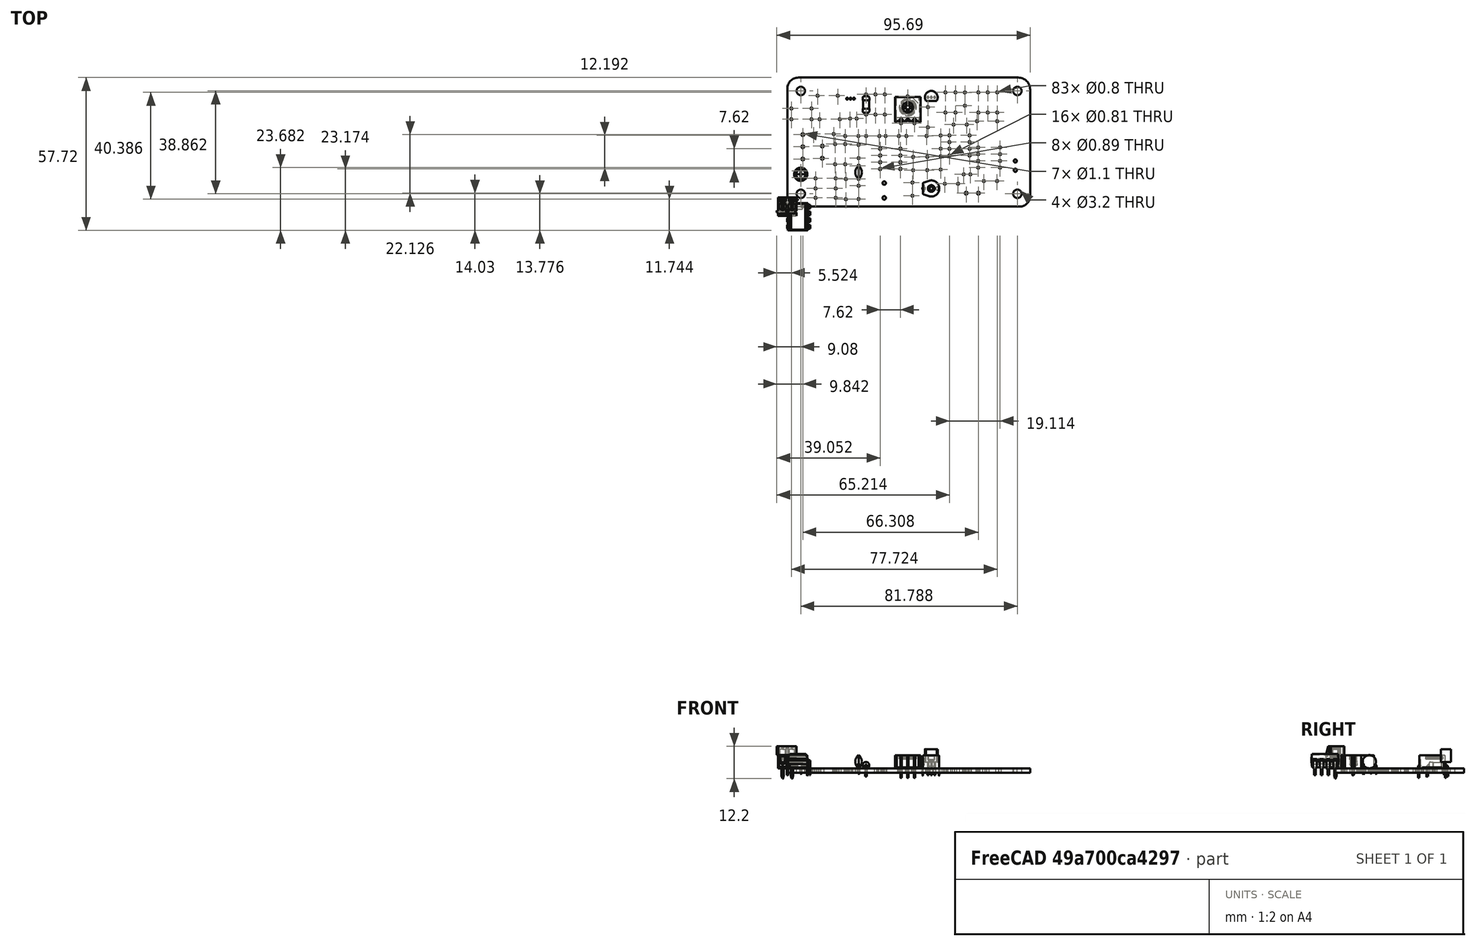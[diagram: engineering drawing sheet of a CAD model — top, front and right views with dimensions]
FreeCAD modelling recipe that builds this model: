
FCSTD DOCUMENT  (FreeCAD 0.19R24267 +148 (Git))
Label: if-and-log-amp-board
License: All rights reserved
LicenseURL: http://en.wikipedia.org/wiki/All_rights_reserved
objects: Part::Feature×57, App::Link×44, App::Part×10, PartDesign::CoordinateSystem×1, Sketcher::SketchObject×1
note: 59 computed .brp shape members not serialized (recipe doc carries the construction recipe); baked Part::Feature solids carry a one-line shape summary decoded from their .brp

FEATURE [PartDesign::CoordinateSystem] Local_CS_cd3
  AttacherType = Attacher::AttachEngine3D
FEATURE [Part::Feature] Pcb_cd3
  Placement = pos=(-95.3516,129.184,0) rot=(0,0,1;0rad)
  shape: bbox 91.69 x 48.77 x 1.6 mm, 140 faces (baked)
FEATURE [Sketcher::SketchObject] PCB_Sketch_cd3
  FullyConstrained = false
  sketch-geometry (8):
    g0: LineSegment StartX=91.694 StartY=3.98868 StartZ=0 EndX=91.694 EndY=44.2582 EndZ=0
    g1: LineSegment StartX=4.55236 StartY=0 StartZ=0 EndX=87.7053 EndY=-2.7e-15 EndZ=0
    g2: LineSegment StartX=0 StartY=44.5614 StartZ=0 EndX=0 EndY=4.55236 EndZ=0
    g3: LineSegment StartX=87.1842 StartY=48.768 StartZ=0 EndX=4.20659 EndY=48.768 EndZ=0
    g4: ArcOfCircle CenterX=4.20659 CenterY=44.5614 CenterZ=0 NormalX=0 NormalY=0 NormalZ=-1 AngleXU=1.7676e-08 Radius=4.20659 StartAngle=0 EndAngle=1.5708
    g5: ArcOfCircle CenterX=87.7053 CenterY=3.98868 CenterZ=0 NormalX=0 NormalY=0 NormalZ=-1 AngleXU=-3.14159 Radius=3.98868 StartAngle=0 EndAngle=1.5708
    g6: ArcOfCircle CenterX=4.55236 CenterY=4.55236 CenterZ=0 NormalX=0 NormalY=0 NormalZ=-1 AngleXU=-1.5708 Radius=4.55236 StartAngle=0 EndAngle=1.5708
    g7: ArcOfCircle CenterX=87.1842 CenterY=44.2582 CenterZ=0 NormalX=0 NormalY=0 NormalZ=-1 AngleXU=1.5708 Radius=4.50978 StartAngle=0 EndAngle=1.5708
  constraints (8):
    c: Coincident(g2,g6)
    c: Coincident(g2,g4)
    c: Coincident(g3,g4)
    c: Coincident(g1,g6)
    c: Coincident(g3,g7)
    c: Coincident(g1,g5)
    c: Coincident(g0,g5)
    c: Coincident(g0,g7)
FEATURE [Part::Feature] Shape  label="R312_R_Axial_DIN0207_L63mm_D25mm_P762mm_Horizontal_d8800c764c18"
  Placement = pos=(29.718,42.418,0) rot=(0,0,-1;1.5708rad)
  shape: bbox 2.706 x 8.418 x 5.603 mm, 15 faces (baked)
FEATURE [App::Link] R312_R_Axial_DIN0207_L63mm_D25mm_P762mm_Horizontal_d8800c764c18_ln_  label="R317_R_Axial_DIN0207_L63mm_D25mm_P762mm_Horizontal_4018a25076d7"
  LinkPlacement = pos=(53.086,37.592,0) rot=(0,0,-1;1.5708rad)
  LinkedObject = -> Shape
  Placement = pos=(53.086,37.592,0) rot=(0,0,-1;1.5708rad)
FEATURE [Part::Feature] Part__Feature  label="T37-6 IND"
  Placement = pos=(0,-2.7,-0.5) rot=(1,0,0;1.5708rad)
  shape: bbox 10.32 x 3.252 x 10.32 mm, 8 faces, 0 solids (baked)
FEATURE [Part::Feature] Part__Feature001  label="T37-6 IND001"
  Placement = pos=(0,-2.7,-0.5) rot=(1,0,0;1.5708rad)
  shape: bbox 10.51 x 3.773 x 9.618 mm, 81 faces, 0 solids (baked)
FEATURE [Part::Feature] Part__Feature002  label="T37-6 IND002"
  Placement = pos=(0,-2.7,-0.5) rot=(1,0,0;1.5708rad)
  shape: bbox 2.23 x 4.584 x 1.894 mm, 1 faces, 0 solids (baked)
FEATURE [Part::Feature] Part__Feature003  label="T37-6 IND003"
  Placement = pos=(0,-2.7,-0.5) rot=(1,0,0;1.5708rad)
  shape: bbox 1.873 x 4.219 x 1.831 mm, 1 faces, 0 solids (baked)
FEATURE [App::Part] T37_6_IND004  label="L301_T37-6 IND004_d27579fe3735"
  Group = -> [Part__Feature,Part__Feature001,Part__Feature002,Part__Feature003]
  Origin = -> Origin008
  Placement = pos=(36.576,8.89,0) rot=(0,0,1;0rad)
FEATURE [App::Link] L301_T37_6_IND004_d27579fe3735_ln_  label="L301_T37-6 IND004_d27579fe3735[2]"
  LinkPlacement = pos=(36.576,8.89,0) rot=(0,0,1;0rad)
  LinkedObject = -> T37_6_IND004
  Placement = pos=(36.576,8.89,0) rot=(0,0,1;0rad)
FEATURE [App::Link] R312_R_Axial_DIN0207_L63mm_D25mm_P762mm_Horizontal_d8800c764c18_ln_001  label="R311_R_Axial_DIN0207_L63mm_D25mm_P762mm_Horizontal_eb464a22a280"
  LinkPlacement = pos=(63.5,35.56,0) rot=(0,0,1;1.5708rad)
  LinkedObject = -> Shape
  Placement = pos=(63.5,35.56,0) rot=(0,0,1;1.5708rad)
FEATURE [Part::Feature] Shape001  label="C305_C_Disc_D50mm_W25mm_P500mm_af24686a53ab"
  Placement = pos=(26.924,10.454,0) rot=(0,0,1;1.5708rad)
  shape: bbox 2.5 x 5.5 x 7.1 mm, 10 faces (baked)
FEATURE [Part::Feature] Part__Feature004  label="part"
  shape: bbox 0.374 x 0.374 x 0.003 mm, 3 faces (baked)
FEATURE [Part::Feature] Part__Feature005  label="part001"
  shape: bbox 7.484 x 10.29 x 3.559 mm, 14 faces (baked)
FEATURE [Part::Feature] Part__Feature006  label="part002"
  shape: bbox 0.255 x 1.32 x 6.096 mm, 12 faces (baked)
FEATURE [Part::Feature] Part__Feature007  label="part003"
  shape: bbox 0.255 x 1.32 x 6.096 mm, 12 faces (baked)
FEATURE [Part::Feature] Part__Feature008  label="part004"
  shape: bbox 0.255 x 1.32 x 6.096 mm, 12 faces (baked)
FEATURE [Part::Feature] Part__Feature009  label="part005"
  shape: bbox 0.255 x 1.32 x 6.096 mm, 12 faces (baked)
FEATURE [Part::Feature] Part__Feature010  label="part006"
  shape: bbox 0.255 x 1.32 x 6.096 mm, 12 faces (baked)
FEATURE [Part::Feature] Part__Feature011  label="part007"
  shape: bbox 0.255 x 1.32 x 6.096 mm, 12 faces (baked)
FEATURE [Part::Feature] Part__Feature012  label="part008"
  shape: bbox 0.255 x 1.32 x 6.096 mm, 12 faces (baked)
FEATURE [Part::Feature] Part__Feature013  label="part009"
  shape: bbox 0.255 x 1.32 x 6.096 mm, 12 faces (baked)
FEATURE [App::Part] part010  label="U301_part010_b2ee337b9778"
  Group = -> [Part__Feature004,Part__Feature005,Part__Feature006,Part__Feature007,Part__Feature008,Part__Feature009,Part__Feature010,Part__Feature011,Part__Feature012,Part__Feature013]
  Origin = -> Origin009
  Placement = pos=(35.052,21.844,0) rot=(0,0,1;0rad)
FEATURE [App::Link] U301_part010_b2ee337b9778_ln_  label="U301_part010_b2ee337b9778[2]"
  LinkPlacement = pos=(35.052,21.844,0) rot=(0,0,1;0rad)
  LinkedObject = -> part010
  Placement = pos=(35.052,21.844,0) rot=(0,0,1;0rad)
FEATURE [App::Link] C305_C_Disc_D50mm_W25mm_P500mm_af24686a53ab_ln_  label="C314_C_Disc_D50mm_W25mm_P500mm_66019c48ab44"
  LinkPlacement = pos=(52.832,18.796,0) rot=(0,0,-1;1.5708rad)
  LinkedObject = -> Shape001
  Placement = pos=(52.832,18.796,0) rot=(0,0,-1;1.5708rad)
FEATURE [App::Link] R312_R_Axial_DIN0207_L63mm_D25mm_P762mm_Horizontal_d8800c764c18_ln_002  label="R310_R_Axial_DIN0207_L63mm_D25mm_P762mm_Horizontal_05b3165d4c12"
  LinkPlacement = pos=(21.844,16.002,0) rot=(0,0,1;1.5708rad)
  LinkedObject = -> Shape
  Placement = pos=(21.844,16.002,0) rot=(0,0,1;1.5708rad)
FEATURE [App::Link] R312_R_Axial_DIN0207_L63mm_D25mm_P762mm_Horizontal_d8800c764c18_ln_003  label="R303_R_Axial_DIN0207_L63mm_D25mm_P762mm_Horizontal_ac0d1b4e9247"
  LinkPlacement = pos=(22.098,10.414,0) rot=(0,0,-1;1.5708rad)
  LinkedObject = -> Shape
  Placement = pos=(22.098,10.414,0) rot=(0,0,-1;1.5708rad)
FEATURE [App::Link] R312_R_Axial_DIN0207_L63mm_D25mm_P762mm_Horizontal_d8800c764c18_ln_004  label="R308_R_Axial_DIN0207_L63mm_D25mm_P762mm_Horizontal_420d2e1cb67d"
  LinkPlacement = pos=(17.526,27.432,0) rot=(0,0,1;3.14159rad)
  LinkedObject = -> Shape
  Placement = pos=(17.526,27.432,0) rot=(0,0,1;3.14159rad)
FEATURE [App::Link] C305_C_Disc_D50mm_W25mm_P500mm_af24686a53ab_ln_001  label="C307_C_Disc_D50mm_W25mm_P500mm_d277bf6e893d"
  LinkPlacement = pos=(21.844,26.67,0) rot=(0,0,1;0rad)
  LinkedObject = -> Shape001
  Placement = pos=(21.844,26.67,0) rot=(0,0,1;0rad)
FEATURE [App::Link] C305_C_Disc_D50mm_W25mm_P500mm_af24686a53ab_ln_002  label="C322_C_Disc_D50mm_W25mm_P500mm_8be9586b07ae"
  LinkPlacement = pos=(74.208,9.652,0) rot=(0,0,1;0rad)
  LinkedObject = -> Shape001
  Placement = pos=(74.208,9.652,0) rot=(0,0,1;0rad)
FEATURE [App::Link] C305_C_Disc_D50mm_W25mm_P500mm_af24686a53ab_ln_003  label="C318_C_Disc_D50mm_W25mm_P500mm_bcd050c28ec2"
  LinkPlacement = pos=(57.912,21.884,0) rot=(0,0,1;1.5708rad)
  LinkedObject = -> Shape001
  Placement = pos=(57.912,21.884,0) rot=(0,0,1;1.5708rad)
FEATURE [App::Link] R312_R_Axial_DIN0207_L63mm_D25mm_P762mm_Horizontal_d8800c764c18_ln_005  label="R313_R_Axial_DIN0207_L63mm_D25mm_P762mm_Horizontal_88b099f6b6af"
  LinkPlacement = pos=(44.958,26.67,0) rot=(0,0,1;0rad)
  LinkedObject = -> Shape
  Placement = pos=(44.958,26.67,0) rot=(0,0,1;0rad)
FEATURE [Part::Feature] Part__Feature014  label="D_DO-35_SOD27_P7.62mm_Horizontal"
  shape: bbox 8.244 x 0.5 x 4.312 mm, 7 faces (baked)
FEATURE [Part::Feature] Part__Feature015  label="D_DO-35_SOD27_P7.62mm_Horizontal001"
  shape: bbox 4 x 2.165 x 2.165 mm, 9 faces (baked)
FEATURE [App::Part] D_DO_35_SOD27_P7_62mm_Horizontal  label="D301_D_DO-35_SOD27_P7.62mm_Horizontal002_327d4bbba91b"
  Group = -> [Part__Feature014,Part__Feature015]
  Origin = -> Origin010
  Placement = pos=(36.83,42.418,0) rot=(0,0,-1;1.5708rad)
FEATURE [Part::Feature] Shape002  label="C315_Trimmer Cap - Brown_147f20cc58c8"
  Placement = pos=(51.562,6.858,0) rot=(0,0,1;0rad)
  shape: bbox 6.858 x 6.618 x 7.625 mm, 264 faces (baked)
FEATURE [App::Link] C315_Trimmer_Cap___Brown_147f20cc58c8_ln_  label="C315_Trimmer Cap - Brown_147f20cc58c8[2]"
  LinkPlacement = pos=(51.562,6.858,0) rot=(0,0,1;0rad)
  LinkedObject = -> Shape002
  Placement = pos=(51.562,6.858,0) rot=(0,0,1;0rad)
FEATURE [App::Link] C305_C_Disc_D50mm_W25mm_P500mm_af24686a53ab_ln_004  label="C316_C_Disc_D50mm_W25mm_P500mm_439d64aa2155"
  LinkPlacement = pos=(47.244,4.104,0) rot=(0,0,1;1.5708rad)
  LinkedObject = -> Shape001
  Placement = pos=(47.244,4.104,0) rot=(0,0,1;1.5708rad)
FEATURE [Part::Feature] Shape003  label="C304_CP_Radial_D50mm_P250mm_152b455e995b"
  Placement = pos=(5.08,10.9869,0) rot=(0,0,1;1.5708rad)
  shape: bbox 6.515 x 6.128 x 7 mm, 49 faces (baked)
FEATURE [Part::Feature] Part__Feature016  label="part010"
  shape: bbox 0.3556 x 0.3556 x 0.003 mm, 3 faces (baked)
FEATURE [Part::Feature] Part__Feature017  label="part011"
  shape: bbox 7.118 x 10.16 x 5.084 mm, 14 faces (baked)
FEATURE [Part::Feature] Part__Feature018  label="part012"
  shape: bbox 0.825 x 1.32 x 5.588 mm, 12 faces (baked)
FEATURE [Part::Feature] Part__Feature019  label="part013"
  shape: bbox 0.825 x 1.32 x 5.588 mm, 12 faces (baked)
FEATURE [Part::Feature] Part__Feature020  label="part014"
  shape: bbox 0.825 x 1.32 x 5.588 mm, 12 faces (baked)
FEATURE [Part::Feature] Part__Feature021  label="part015"
  shape: bbox 0.825 x 1.32 x 5.588 mm, 12 faces (baked)
FEATURE [Part::Feature] Part__Feature022  label="part016"
  shape: bbox 0.826 x 1.32 x 5.588 mm, 12 faces (baked)
FEATURE [Part::Feature] Part__Feature023  label="part017"
  shape: bbox 0.826 x 1.32 x 5.588 mm, 12 faces (baked)
FEATURE [Part::Feature] Part__Feature024  label="part018"
  shape: bbox 0.826 x 1.32 x 5.588 mm, 12 faces (baked)
FEATURE [Part::Feature] Part__Feature025  label="part019"
  shape: bbox 0.826 x 1.32 x 5.588 mm, 12 faces (baked)
FEATURE [App::Part] CA3140EZ  label="U305_CA3140EZ_e3195bf92463"
  Group = -> [Part__Feature016,Part__Feature017,Part__Feature018,Part__Feature019,Part__Feature020,Part__Feature021,Part__Feature022,Part__Feature023,Part__Feature024,Part__Feature025]
  Origin = -> Origin011
  Placement = pos=(72.0725,22.352,0) rot=(0,0,1;0rad)
FEATURE [App::Link] U305_CA3140EZ_e3195bf92463_ln_  label="U305_CA3140EZ_e3195bf92463[2]"
  LinkPlacement = pos=(72.0725,22.352,0) rot=(0,0,1;0rad)
  LinkedObject = -> CA3140EZ
  Placement = pos=(72.0725,22.352,0) rot=(0,0,1;0rad)
FEATURE [App::Link] R312_R_Axial_DIN0207_L63mm_D25mm_P762mm_Horizontal_d8800c764c18_ln_006  label="R320_R_Axial_DIN0207_L63mm_D25mm_P762mm_Horizontal_ad0762ac8e56"
  LinkPlacement = pos=(75.692,35.56,0) rot=(0,0,1;1.5708rad)
  LinkedObject = -> Shape
  Placement = pos=(75.692,35.56,0) rot=(0,0,1;1.5708rad)
FEATURE [App::Link] R312_R_Axial_DIN0207_L63mm_D25mm_P762mm_Horizontal_d8800c764c18_ln_007  label="R307_R_Axial_DIN0207_L63mm_D25mm_P762mm_Horizontal_e76c4267341d"
  LinkPlacement = pos=(10.668,3.302,0) rot=(0,0,1;0rad)
  LinkedObject = -> Shape
  Placement = pos=(10.668,3.302,0) rot=(0,0,1;0rad)
FEATURE [Part::Feature] Part__Feature026  label="part020"
  shape: bbox 0.3556 x 0.3556 x 0.003 mm, 3 faces (baked)
FEATURE [Part::Feature] Part__Feature027  label="part021"
  shape: bbox 7.115 x 10.16 x 4.956 mm, 14 faces (baked)
FEATURE [Part::Feature] Part__Feature028  label="part022"
  shape: bbox 0.508 x 1.32 x 5.652 mm, 12 faces (baked)
FEATURE [Part::Feature] Part__Feature029  label="part023"
  shape: bbox 0.508 x 1.32 x 5.652 mm, 12 faces (baked)
FEATURE [Part::Feature] Part__Feature030  label="part024"
  shape: bbox 0.508 x 1.32 x 5.652 mm, 12 faces (baked)
FEATURE [Part::Feature] Part__Feature031  label="part025"
  shape: bbox 0.508 x 1.32 x 5.652 mm, 12 faces (baked)
FEATURE [Part::Feature] Part__Feature032  label="part026"
  shape: bbox 0.508 x 1.32 x 5.652 mm, 12 faces (baked)
FEATURE [Part::Feature] Part__Feature033  label="part027"
  shape: bbox 0.508 x 1.32 x 5.652 mm, 12 faces (baked)
FEATURE [Part::Feature] Part__Feature034  label="part028"
  shape: bbox 0.508 x 1.32 x 5.652 mm, 12 faces (baked)
FEATURE [Part::Feature] Part__Feature035  label="part029"
  shape: bbox 0.508 x 1.32 x 5.652 mm, 12 faces (baked)
FEATURE [App::Part] ad8307  label="U304_ad8307_c593cb31029a"
  Group = -> [Part__Feature026,Part__Feature027,Part__Feature028,Part__Feature029,Part__Feature030,Part__Feature031,Part__Feature032,Part__Feature033,Part__Feature034,Part__Feature035]
  Origin = -> Origin012
  Placement = pos=(68.834,19.304,0) rot=(0,0,1;3.14159rad)
FEATURE [App::Link] U304_ad8307_c593cb31029a_ln_  label="U304_ad8307_c593cb31029a[2]"
  LinkPlacement = pos=(68.834,19.304,0) rot=(0,0,1;3.14159rad)
  LinkedObject = -> ad8307
  Placement = pos=(68.834,19.304,0) rot=(0,0,1;3.14159rad)
FEATURE [App::Link] C304_CP_Radial_D50mm_P250mm_152b455e995b_ln_  label="C321_CP_Radial_D50mm_P250mm_d0c01afd2d31"
  LinkPlacement = pos=(66.6129,12.192,0) rot=(0,0,1;0rad)
  LinkedObject = -> Shape003
  Placement = pos=(66.6129,12.192,0) rot=(0,0,1;0rad)
FEATURE [App::Link] R312_R_Axial_DIN0207_L63mm_D25mm_P762mm_Horizontal_d8800c764c18_ln_008  label="R305_R_Axial_DIN0207_L63mm_D25mm_P762mm_Horizontal_0d6a1a2448f2"
  LinkPlacement = pos=(1.524,33.02,0) rot=(0,0,1;0rad)
  LinkedObject = -> Shape
  Placement = pos=(1.524,33.02,0) rot=(0,0,1;0rad)
FEATURE [App::Link] C305_C_Disc_D50mm_W25mm_P500mm_af24686a53ab_ln_005  label="C309_C_Disc_D50mm_W25mm_P500mm_fd599f2c4c1b"
  LinkPlacement = pos=(62.778,30.988,0) rot=(0,0,1;0rad)
  LinkedObject = -> Shape001
  Placement = pos=(62.778,30.988,0) rot=(0,0,1;0rad)
FEATURE [Part::Feature] Shape004  label="RV302_33756-68028_1ee07bcbfc79"
  Placement = pos=(48.006,31.811,0) rot=(0,0,1;1.5708rad)
  shape: bbox 9.959 x 11.1 x 8.691 mm, 205 faces (baked)
FEATURE [App::Link] RV302_33756_68028_1ee07bcbfc79_ln_  label="RV302_33756-68028_1ee07bcbfc79[2]"
  LinkPlacement = pos=(48.006,31.811,0) rot=(0,0,1;1.5708rad)
  LinkedObject = -> Shape004
  Placement = pos=(48.006,31.811,0) rot=(0,0,1;1.5708rad)
FEATURE [App::Link] C305_C_Disc_D50mm_W25mm_P500mm_af24686a53ab_ln_006  label="C320_C_Disc_D50mm_W25mm_P500mm_43840d42c864"
  LinkPlacement = pos=(59.476,8.636,0) rot=(0,0,1;0rad)
  LinkedObject = -> Shape001
  Placement = pos=(59.476,8.636,0) rot=(0,0,1;0rad)
FEATURE [App::Link] R312_R_Axial_DIN0207_L63mm_D25mm_P762mm_Horizontal_d8800c764c18_ln_009  label="R321_R_Axial_DIN0207_L63mm_D25mm_P762mm_Horizontal_5cb9c9a7e22a"
  LinkPlacement = pos=(72.136,35.56,0) rot=(0,0,1;1.5708rad)
  LinkedObject = -> Shape
  Placement = pos=(72.136,35.56,0) rot=(0,0,1;1.5708rad)
FEATURE [App::Link] R312_R_Axial_DIN0207_L63mm_D25mm_P762mm_Horizontal_d8800c764c18_ln_010  label="R315_R_Axial_DIN0207_L63mm_D25mm_P762mm_Horizontal_c86d6ec5e1ed"
  LinkPlacement = pos=(33.274,34.798,0) rot=(0,0,1;1.5708rad)
  LinkedObject = -> Shape
  Placement = pos=(33.274,34.798,0) rot=(0,0,1;1.5708rad)
FEATURE [App::Link] C305_C_Disc_D50mm_W25mm_P500mm_af24686a53ab_ln_007  label="C311_C_Disc_D50mm_W25mm_P500mm_3edbdc47b6ee"
  LinkPlacement = pos=(47.498,13.756,0) rot=(0,0,1;1.5708rad)
  LinkedObject = -> Shape001
  Placement = pos=(47.498,13.756,0) rot=(0,0,1;1.5708rad)
FEATURE [App::Link] R312_R_Axial_DIN0207_L63mm_D25mm_P762mm_Horizontal_d8800c764c18_ln_011  label="R302_R_Axial_DIN0207_L63mm_D25mm_P762mm_Horizontal_ca0fd10d098d"
  LinkPlacement = pos=(10.668,6.858,0) rot=(0,0,1;0rad)
  LinkedObject = -> Shape
  Placement = pos=(10.668,6.858,0) rot=(0,0,1;0rad)
FEATURE [App::Link] C304_CP_Radial_D50mm_P250mm_152b455e995b_ln_001  label="C313_CP_Radial_D50mm_P250mm_09f3f0dc9b60"
  LinkPlacement = pos=(23.6869,33.274,0) rot=(0,0,1;0rad)
  LinkedObject = -> Shape003
  Placement = pos=(23.6869,33.274,0) rot=(0,0,1;0rad)
FEATURE [App::Link] C305_C_Disc_D50mm_W25mm_P500mm_af24686a53ab_ln_008  label="C308_C_Disc_D50mm_W25mm_P500mm_c3ac8cc940d8"
  LinkPlacement = pos=(26.924,18.328,0) rot=(0,0,1;1.5708rad)
  LinkedObject = -> Shape001
  Placement = pos=(26.924,18.328,0) rot=(0,0,1;1.5708rad)
FEATURE [App::Link] C305_C_Disc_D50mm_W25mm_P500mm_af24686a53ab_ln_009  label="C310_C_Disc_D50mm_W25mm_P500mm_f1d4fb98b27c"
  LinkPlacement = pos=(67.056,43.14,0) rot=(0,0,-1;1.5708rad)
  LinkedObject = -> Shape001
  Placement = pos=(67.056,43.14,0) rot=(0,0,-1;1.5708rad)
FEATURE [App::Link] R312_R_Axial_DIN0207_L63mm_D25mm_P762mm_Horizontal_d8800c764c18_ln_012  label="R319_R_Axial_DIN0207_L63mm_D25mm_P762mm_Horizontal_1979a6faa688"
  LinkPlacement = pos=(79.248,32.258,0) rot=(0,0,1;3.14159rad)
  LinkedObject = -> Shape
  Placement = pos=(79.248,32.258,0) rot=(0,0,1;3.14159rad)
FEATURE [App::Link] R312_R_Axial_DIN0207_L63mm_D25mm_P762mm_Horizontal_d8800c764c18_ln_013  label="R301_R_Axial_DIN0207_L63mm_D25mm_P762mm_Horizontal_2227cb83239a"
  LinkPlacement = pos=(10.668,10.668,0) rot=(0,0,1;0rad)
  LinkedObject = -> Shape
  Placement = pos=(10.668,10.668,0) rot=(0,0,1;0rad)
FEATURE [App::Link] C305_C_Disc_D50mm_W25mm_P500mm_af24686a53ab_ln_010  label="C312_C_Disc_D50mm_W25mm_P500mm_d65cbd7c44b7"
  LinkPlacement = pos=(29.758,26.67,0) rot=(0,0,1;0rad)
  LinkedObject = -> Shape001
  Placement = pos=(29.758,26.67,0) rot=(0,0,1;0rad)
FEATURE [Part::Feature] Shape005  label="U302_TO-92_Inline_Narrow_4b0f5a09eaed"
  Placement = pos=(53.086,41.296,0) rot=(0,0,1;0rad)
  shape: bbox 4.83 x 3.745 x 9.8 mm, 19 faces (baked)
FEATURE [App::Link] R312_R_Axial_DIN0207_L63mm_D25mm_P762mm_Horizontal_d8800c764c18_ln_014  label="R309_R_Axial_DIN0207_L63mm_D25mm_P762mm_Horizontal_01de069d222f"
  LinkPlacement = pos=(18.034,23.622,0) rot=(0,0,-1;1.5708rad)
  LinkedObject = -> Shape
  Placement = pos=(18.034,23.622,0) rot=(0,0,-1;1.5708rad)
FEATURE [App::Link] C305_C_Disc_D50mm_W25mm_P500mm_af24686a53ab_ln_011  label="C306_C_Disc_D50mm_W25mm_P500mm_10b0299ea321"
  LinkPlacement = pos=(26.924,2.874,0) rot=(0,0,1;1.5708rad)
  LinkedObject = -> Shape001
  Placement = pos=(26.924,2.874,0) rot=(0,0,1;1.5708rad)
FEATURE [App::Link] R312_R_Axial_DIN0207_L63mm_D25mm_P762mm_Horizontal_d8800c764c18_ln_015  label="R316_R_Axial_DIN0207_L63mm_D25mm_P762mm_Horizontal_74c034375f1f"
  LinkPlacement = pos=(59.69,35.56,0) rot=(0,0,1;1.5708rad)
  LinkedObject = -> Shape
  Placement = pos=(59.69,35.56,0) rot=(0,0,1;1.5708rad)
FEATURE [App::Link] R312_R_Axial_DIN0207_L63mm_D25mm_P762mm_Horizontal_d8800c764c18_ln_016  label="R304_R_Axial_DIN0207_L63mm_D25mm_P762mm_Horizontal_d1494d8a4bbd"
  LinkPlacement = pos=(9.144,37.084,0) rot=(0,0,1;3.14159rad)
  LinkedObject = -> Shape
  Placement = pos=(9.144,37.084,0) rot=(0,0,1;3.14159rad)
FEATURE [App::Link] C305_C_Disc_D50mm_W25mm_P500mm_af24686a53ab_ln_012  label="C319_C_Disc_D50mm_W25mm_P500mm_13615241f1cc"
  LinkPlacement = pos=(37.124,26.67,0) rot=(0,0,1;0rad)
  LinkedObject = -> Shape001
  Placement = pos=(37.124,26.67,0) rot=(0,0,1;0rad)
FEATURE [App::Link] U302_TO_92_Inline_Narrow_4b0f5a09eaed_ln_  label="U303_TO-92_Inline_Narrow_5c8ffa349c7f"
  LinkPlacement = pos=(22.606,40.788,0) rot=(0,0,1;0rad)
  LinkedObject = -> Shape005
  Placement = pos=(22.606,40.788,0) rot=(0,0,1;0rad)
FEATURE [App::Link] C305_C_Disc_D50mm_W25mm_P500mm_af24686a53ab_ln_013  label="C317_C_Disc_D50mm_W25mm_P500mm_e25e1232d7e5"
  LinkPlacement = pos=(57.912,14.01,0) rot=(0,0,1;1.5708rad)
  LinkedObject = -> Shape001
  Placement = pos=(57.912,14.01,0) rot=(0,0,1;1.5708rad)
FEATURE [App::Link] R312_R_Axial_DIN0207_L63mm_D25mm_P762mm_Horizontal_d8800c764c18_ln_017  label="R314_R_Axial_DIN0207_L63mm_D25mm_P762mm_Horizontal_c4f5a1a52bcc"
  LinkPlacement = pos=(19.05,41.91,0) rot=(0,0,1;3.14159rad)
  LinkedObject = -> Shape
  Placement = pos=(19.05,41.91,0) rot=(0,0,1;3.14159rad)
FEATURE [App::Link] R312_R_Axial_DIN0207_L63mm_D25mm_P762mm_Horizontal_d8800c764c18_ln_018  label="R306_R_Axial_DIN0207_L63mm_D25mm_P762mm_Horizontal_2c74f60fcb90"
  LinkPlacement = pos=(12.192,33.02,0) rot=(0,0,1;0rad)
  LinkedObject = -> Shape
  Placement = pos=(12.192,33.02,0) rot=(0,0,1;0rad)
FEATURE [App::Link] R312_R_Axial_DIN0207_L63mm_D25mm_P762mm_Horizontal_d8800c764c18_ln_019  label="R318_R_Axial_DIN0207_L63mm_D25mm_P762mm_Horizontal_b4ffca175b66"
  LinkPlacement = pos=(79.248,35.56,0) rot=(0,0,1;1.5708rad)
  LinkedObject = -> Shape
  Placement = pos=(79.248,35.56,0) rot=(0,0,1;1.5708rad)
FEATURE [Part::Feature] Part__Feature036  label="SOLID"
  Placement = pos=(0,0,4.2) rot=(0,0,1;0rad)
  shape: bbox 8 x 7 x 8.4 mm, 72 faces (baked)
FEATURE [Part::Feature] Part__Feature037  label="SOLID001"
  Placement = pos=(0,0,4.2) rot=(0,0,1;0rad)
  shape: bbox 2.75 x 3.75 x 8.15 mm, 17 faces (baked)
FEATURE [Part::Feature] Part__Feature038  label="SOLID002"
  Placement = pos=(0,0,4.2) rot=(0,0,1;0rad)
  shape: bbox 2.75 x 3.75 x 8.15 mm, 17 faces (baked)
FEATURE [Part::Feature] Part__Feature039  label="SOLID003"
  Placement = pos=(0,0,4.2) rot=(0,0,1;0rad)
  shape: bbox 2.9 x 4.5 x 2.65 mm, 46 faces (baked)
FEATURE [Part::Feature] Part__Feature040  label="SOLID004"
  Placement = pos=(0,0,4.2) rot=(0,0,1;0rad)
  shape: bbox 2.9 x 4.5 x 2.65 mm, 46 faces (baked)
FEATURE [Part::Feature] Part__Feature041  label="SOLID005"
  Placement = pos=(0,0,4.2) rot=(0,0,1;0rad)
  shape: bbox 3.139 x 3.139 x 4.6 mm, 17 faces (baked)
FEATURE [Part::Feature] Part__Feature042  label="SOLID006"
  Placement = pos=(0,0,4.2) rot=(0,0,1;0rad)
  shape: bbox 3.139 x 3.139 x 4.6 mm, 17 faces (baked)
FEATURE [App::Part] _91103110002_1  label="J306_691103110002_1_2eef4a563ef5"
  Group = -> [Part__Feature036,Part__Feature037,Part__Feature038,Part__Feature039,Part__Feature040,Part__Feature041,Part__Feature042]
  Origin = -> Origin013
  Placement = pos=(86.106,15.494,0) rot=(0,0,1;1.5708rad)
FEATURE [App::Link] J306_691103110002_1_2eef4a563ef5_ln_  label="J306_691103110002_1_2eef4a563ef5[2]"
  LinkPlacement = pos=(86.106,15.494,4.445) rot=(0,0,1;1.5708rad)
  LinkedObject = -> _91103110002_1
  Placement = pos=(86.106,15.494,4.445) rot=(0,0,1;1.5708rad)
FEATURE [App::Part] Top_cd3
  Group = -> [Shape,R312_R_Axial_DIN0207_L63mm_D25mm_P762mm_Horizontal_d8800c764c18_ln_,T37_6_IND004,L301_T37_6_IND004_d27579fe3735_ln_,R312_R_Axial_DIN0207_L63mm_D25mm_P762mm_Horizontal_d8800c764c18_ln_001,Shape001,part010,U301_part010_b2ee337b9778_ln_,C305_C_Disc_D50mm_W25mm_P500mm_af24686a53ab_ln_,R312_R_Axial_DIN0207_L63mm_D25mm_P762mm_Horizontal_d8800c764c18_ln_002,+46 more]
  Origin = -> Origin003
FEATURE [App::Part] Step_Models_cd3
  Group = -> [Top_cd3]
  Origin = -> Origin002
FEATURE [Part::Feature] pads_area064001  label="topPads_cd3"
  Placement = pos=(-95.3516,129.184,0.02) rot=(0,0,1;0rad)
  shape: bbox 86.28 x 44.23 x 2e-07 mm, 141 faces, 0 solids (baked)
FEATURE [Part::Feature] Shape006001  label="topTracks_cd3"
  Placement = pos=(-95.3516,129.184,0.01) rot=(0,0,1;0rad)
  shape: bbox 76.26 x 42.79 x 2e-07 mm, 37 faces, 0 solids (baked)
FEATURE [Part::Feature] zones_area001  label="topZones_cd3"
  Placement = pos=(-95.3516,129.184,0.01) rot=(0,0,1;0rad)
  shape: bbox 90.93 x 48.01 x 2e-07 mm, 5 faces, 0 solids (baked)
FEATURE [Part::Feature] pads_area064058001  label="botPads_cd3"
  Placement = pos=(-95.3516,129.184,-1.62) rot=(0,0,1;0rad)
  shape: bbox 86.28 x 41.99 x 2e-07 mm, 133 faces, 0 solids (baked)
FEATURE [Part::Feature] Shape006002001  label="botTracks_cd3"
  Placement = pos=(-95.3516,129.184,-1.61) rot=(0,0,1;0rad)
  shape: bbox 84.38 x 41.26 x 2e-07 mm, 39 faces, 0 solids (baked)
FEATURE [Part::Feature] zones_area002001  label="botZones_cd3"
  Placement = pos=(-95.3516,129.184,-1.61) rot=(0,0,1;0rad)
  shape: bbox 90.93 x 48.01 x 2e-07 mm, 4 faces, 0 solids (baked)
FEATURE [Part::Feature] topSilks_b243
  Placement = pos=(-95.3516,129.184,0.07) rot=(0,0,1;0rad)
  shape: bbox 89.92 x 47.75 x 2e-07 mm, 539 faces, 0 solids (baked)
FEATURE [App::Part] Board_Geoms_cd3
  Group = -> [Local_CS_cd3,Pcb_cd3,PCB_Sketch_cd3,pads_area064001,Shape006001,zones_area001,pads_area064058001,Shape006002001,zones_area002001,topSilks_b243]
  Origin = -> Origin
FEATURE [App::Part] Board_cd3  label="if-and-log-amp"
  Group = -> [Board_Geoms_cd3,Step_Models_cd3]
  Origin = -> Origin001
